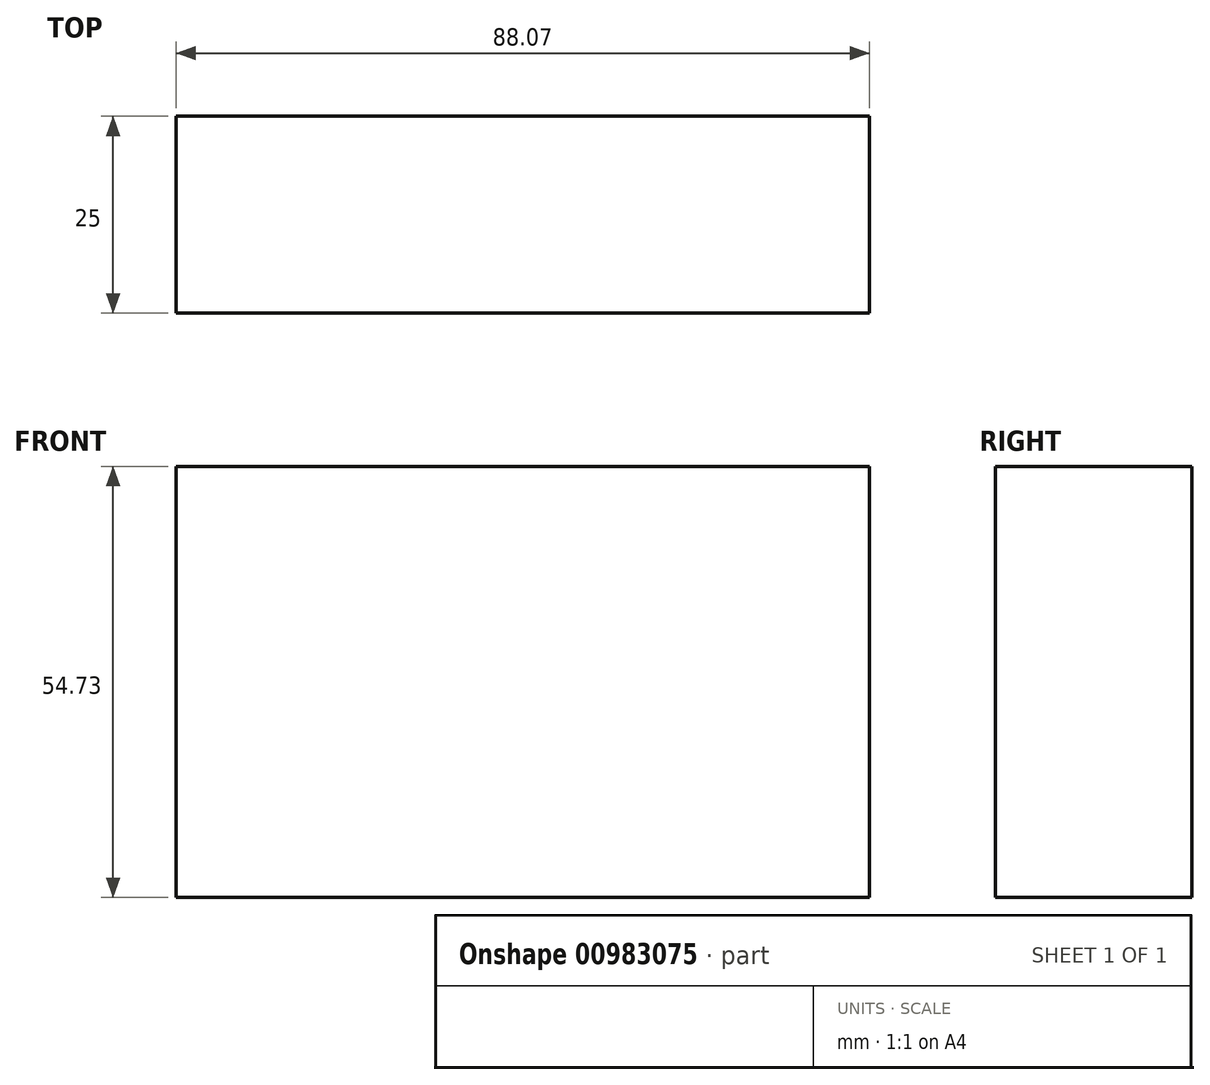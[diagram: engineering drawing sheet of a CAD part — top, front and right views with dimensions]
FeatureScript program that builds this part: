
annotation { "Feature Type Name" : "Feature", "Feature Type Description" : "" }
export const myFeature = defineFeature(function(context is Context, id is Id, definition is map)
    precondition{}
    {
        {
            var Q0;
            Q0=qCreatedBy(makeId("Front.planeOp"),FACE);
            var sketch = newSketch(context, id + "F0", { "sketchPlane" : qUnion([Q0])});
            skLineSegment(sketch, "E0.bottom", {"start": v(-55.25, 50.2) * mm, "end": v(32.82, 50.2) * mm});
            skLineSegment(sketch, "E0.top", {"start": v(-55.25, -4.54) * mm, "end": v(32.82, -4.54) * mm});
            skLineSegment(sketch, "E0.left", {"start": v(-55.25, 50.2) * mm, "end": v(-55.25, -4.54) * mm});
            skLineSegment(sketch, "E0.right", {"start": v(32.82, 50.2) * mm, "end": v(32.82, -4.54) * mm});
            skSolve(sketch);
        }
        {
            var Q0;
            Q0 = qSketchRegion(id + "F0", true);
            extrude(context, id + "F1", {"entities" : qUnion([Q0]), "depth" : 25 * mm, "offsetDistance" : 25 * mm});
        }
    });
